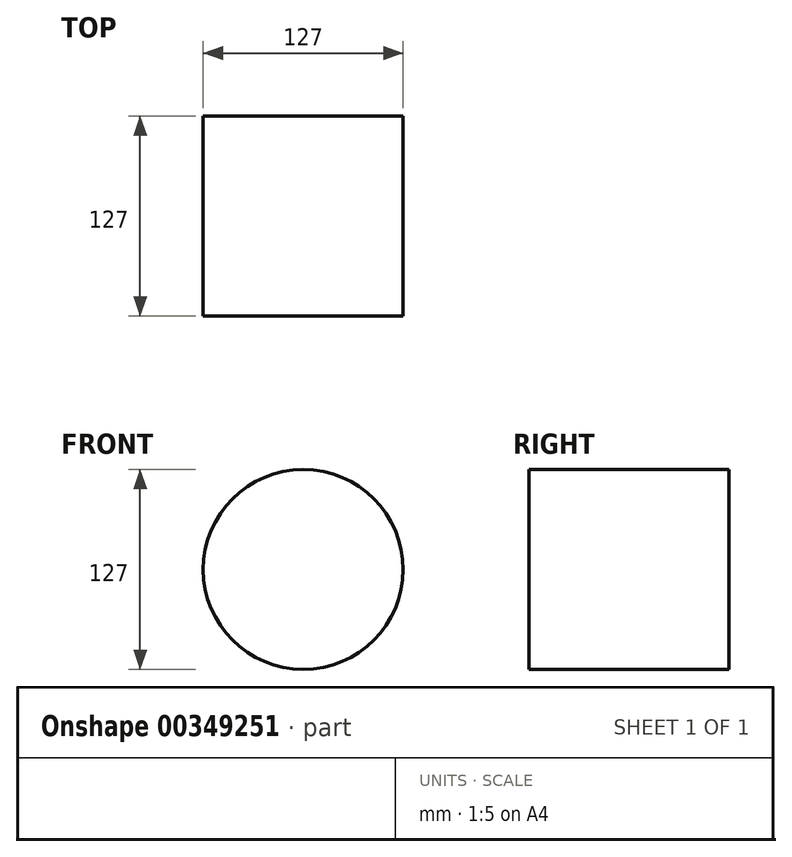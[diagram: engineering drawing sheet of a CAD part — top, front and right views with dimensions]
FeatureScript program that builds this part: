
annotation { "Feature Type Name" : "Feature", "Feature Type Description" : "" }
export const myFeature = defineFeature(function(context is Context, id is Id, definition is map)
    precondition{}
    {
        {
            var Q0;
            Q0=qCreatedBy(makeId("Front.planeOp"),FACE);
            var sketch = newSketch(context, id + "F0", { "sketchPlane" : qUnion([Q0])});
            skCircle(sketch, "E0", {"center": v(-107.46, 10.16) * mm, "radius": 63.5 * mm});
            skSolve(sketch);
        }
        {
            var Q0;
            Q0=makeQuery(id+"F0.imprint","IMPRINT",FACE,{"disambiguationData":[TD([[makeQuery(id+"F0.imprint","IMPRINT",EDGE,{"derivedFrom":sQuery(id+"F0.wireOp",EDGE,"E0")}),1.0]])]});
            extrude(context, id + "F1", {"entities" : qUnion([Q0]), "depth" : 127 * mm});
        }
    });
